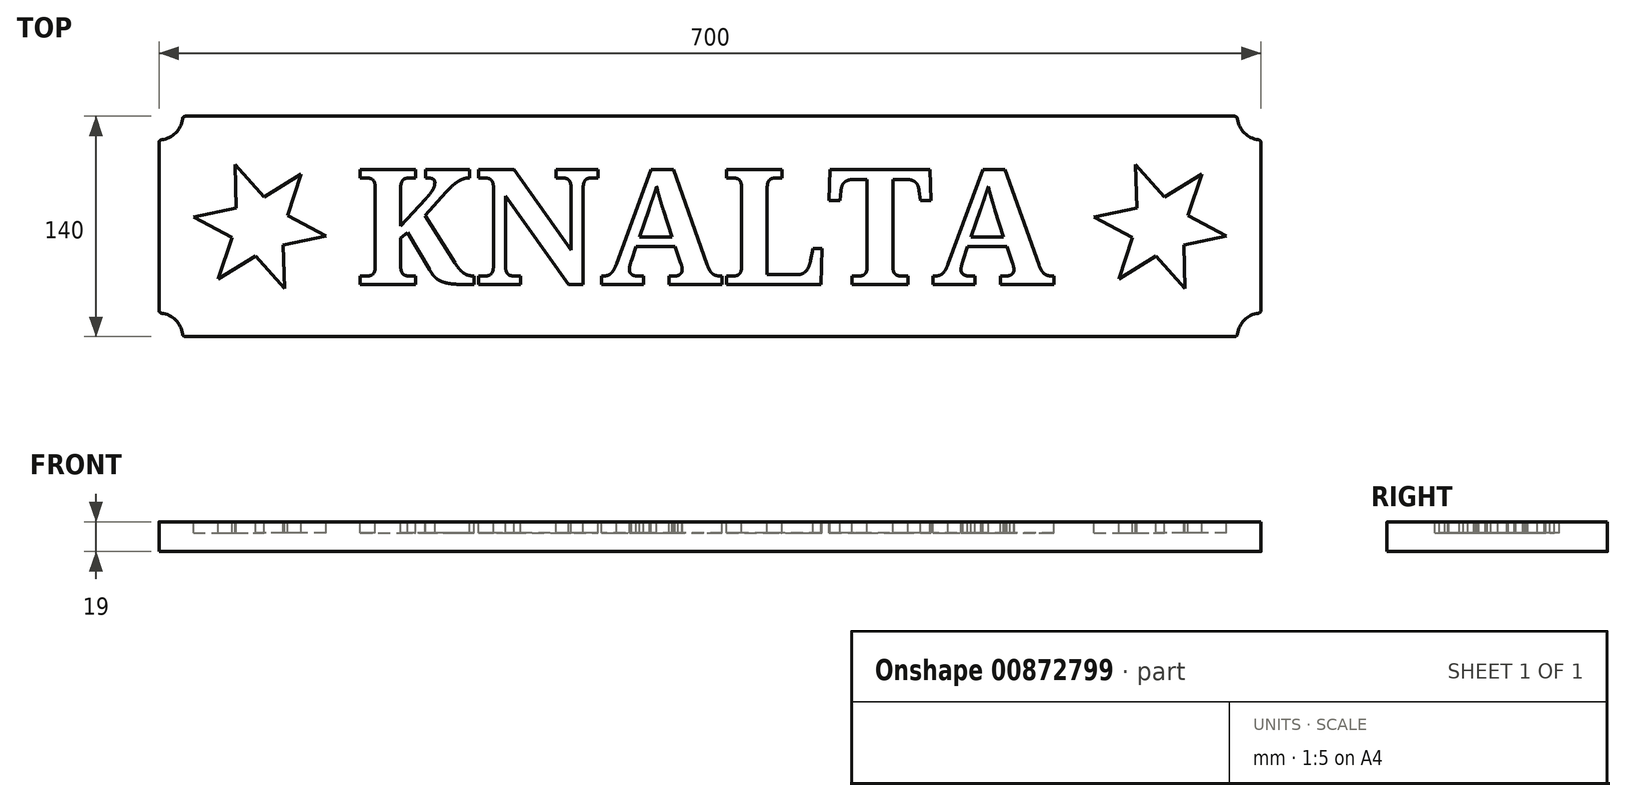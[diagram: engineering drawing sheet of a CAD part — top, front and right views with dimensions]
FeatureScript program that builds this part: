
annotation { "Feature Type Name" : "Feature", "Feature Type Description" : "" }
export const myFeature = defineFeature(function(context is Context, id is Id, definition is map)
    precondition{}
    {
        {
            var Q0;
            Q0=qCreatedBy(makeId("Top.planeOp"),FACE);
            var sketch = newSketch(context, id + "F0", { "sketchPlane" : qUnion([Q0])});
            skLineSegment(sketch, "E0", {"start": v(0, 459.17) * mm, "end": v(0, -526.61) * mm, "construction": true});
            skLineSegment(sketch, "E1", {"start": v(-506.97, 0) * mm, "end": v(534.36, 0) * mm, "construction": true});
            skLineSegment(sketch, "E2.bottom", {"start": v(-333.12, 70) * mm, "end": v(0, 70) * mm});
            skLineSegment(sketch, "E2.top", {"start": v(-350, 0) * mm, "end": v(0, 0) * mm});
            skLineSegment(sketch, "E2.left", {"start": v(-350, 53.12) * mm, "end": v(-350, 0) * mm});
            skLineSegment(sketch, "E2.right", {"start": v(0, 70) * mm, "end": v(0, 0) * mm});
            skArc(sketch, "E3", {"start": v(-348.24, 55.1) * mm, "mid": v(-339.4, 59.4) * mm, "end": v(-335.1, 68.24) * mm});
            skLineSegment(sketch, "E4.MirrorCS", {"start": v(350, 0) * mm, "end": v(0, 0) * mm});
            skLineSegment(sketch, "E5.MirrorCS", {"start": v(333.12, 70) * mm, "end": v(0, 70) * mm});
            skLineSegment(sketch, "E6.MirrorCS", {"start": v(350, 53.12) * mm, "end": v(350, 0) * mm});
            skArc(sketch, "E7.MirrorC", {"start": v(348.24, 55.1) * mm, "mid": v(339.4, 59.4) * mm, "end": v(335.1, 68.24) * mm});
            skLineSegment(sketch, "E8.MirrorCS", {"start": v(0, -70) * mm, "end": v(0, 0) * mm});
            skArc(sketch, "E9.MirrorC", {"start": v(-348.24, -55.1) * mm, "mid": v(-339.4, -59.4) * mm, "end": v(-335.1, -68.24) * mm});
            skLineSegment(sketch, "E10.MirrorCS", {"start": v(-333.12, -70) * mm, "end": v(0, -70) * mm});
            skLineSegment(sketch, "E11.MirrorCS", {"start": v(-350, -53.12) * mm, "end": v(-350, 0) * mm});
            skLineSegment(sketch, "E12.MirrorCS", {"start": v(350, -53.12) * mm, "end": v(350, 0) * mm});
            skLineSegment(sketch, "E13.MirrorCS", {"start": v(333.12, -70) * mm, "end": v(0, -70) * mm});
            skArc(sketch, "E14.MirrorC", {"start": v(348.24, -55.1) * mm, "mid": v(339.4, -59.4) * mm, "end": v(335.1, -68.24) * mm});
            skPoint(sketch, "E15.visualSharp", {"position": v(-335, 70) * mm});
            skArc(sketch, "E15.filletArc", {"start": v(-333.12, 70) * mm, "mid": v(-334.45, 69.5) * mm, "end": v(-335.1, 68.24) * mm});
            skPoint(sketch, "E16.visualSharp", {"position": v(-350, 55) * mm});
            skArc(sketch, "E16.filletArc", {"start": v(-348.24, 55.1) * mm, "mid": v(-349.5, 54.45) * mm, "end": v(-350, 53.12) * mm});
            skPoint(sketch, "E17.visualSharp", {"position": v(-350, -55) * mm});
            skArc(sketch, "E17.filletArc", {"start": v(-350, -53.12) * mm, "mid": v(-349.5, -54.45) * mm, "end": v(-348.24, -55.1) * mm});
            skPoint(sketch, "E18.visualSharp", {"position": v(-335, -70) * mm});
            skArc(sketch, "E18.filletArc", {"start": v(-335.1, -68.24) * mm, "mid": v(-334.45, -69.5) * mm, "end": v(-333.12, -70) * mm});
            skPoint(sketch, "E19.visualSharp", {"position": v(335, -70) * mm});
            skArc(sketch, "E19.filletArc", {"start": v(333.12, -70) * mm, "mid": v(334.45, -69.5) * mm, "end": v(335.1, -68.24) * mm});
            skPoint(sketch, "E20.visualSharp", {"position": v(350, -55) * mm});
            skArc(sketch, "E20.filletArc", {"start": v(348.24, -55.1) * mm, "mid": v(349.5, -54.45) * mm, "end": v(350, -53.12) * mm});
            skPoint(sketch, "E21.visualSharp", {"position": v(350, 55) * mm});
            skArc(sketch, "E21.filletArc", {"start": v(350, 53.12) * mm, "mid": v(349.5, 54.45) * mm, "end": v(348.24, 55.1) * mm});
            skPoint(sketch, "E22.visualSharp", {"position": v(335, 70) * mm});
            skArc(sketch, "E22.filletArc", {"start": v(335.1, 68.24) * mm, "mid": v(334.45, 69.5) * mm, "end": v(333.12, 70) * mm});
            skSolve(sketch);
        }
        {
            var Q0;
            Q0 = qSketchRegion(id + "F0", true);
            extrude(context, id + "F1", {"entities" : qUnion([Q0]), "depth" : 19 * mm, "offsetDistance" : 25 * mm});
        }
        {
            var Q0;
            Q0=makeQuery(id+"F1.opExtrude","CAP_FACE",FACE,{"disambiguationData":[OSD([sQuery(id+"F0.wireOp",EDGE,"E2.bottom"),sQuery(id+"F0.wireOp",EDGE,"E2.left"),sQuery(id+"F0.wireOp",EDGE,"E3"),sQuery(id+"F0.wireOp",EDGE,"E5.MirrorCS"),sQuery(id+"F0.wireOp",EDGE,"E6.MirrorCS"),sQuery(id+"F0.wireOp",EDGE,"E7.MirrorC"),sQuery(id+"F0.wireOp",EDGE,"E9.MirrorC"),sQuery(id+"F0.wireOp",EDGE,"E10.MirrorCS"),sQuery(id+"F0.wireOp",EDGE,"E11.MirrorCS"),sQuery(id+"F0.wireOp",EDGE,"E12.MirrorCS"),sQuery(id+"F0.wireOp",EDGE,"E13.MirrorCS"),sQuery(id+"F0.wireOp",EDGE,"E14.MirrorC")])],"isStart":false});
            var sketch = newSketch(context, id + "F2", { "sketchPlane" : qUnion([Q0])});
            skPoint(sketch, "E23.0.midPoint", {"position": v(-257.12, -22.82) * mm});
            skLineSegment(sketch, "E24", {"start": v(-301.7, 39.5) * mm, "end": v(-300.89, 11.76) * mm});
            skLineSegment(sketch, "E25", {"start": v(-301.7, 39.5) * mm, "end": v(-283.26, 18.78) * mm});
            skLineSegment(sketch, "E26", {"start": v(-328.05, 6.14) * mm, "end": v(-303.63, -7.01) * mm});
            skLineSegment(sketch, "E27", {"start": v(-328.05, 6.14) * mm, "end": v(-300.89, 11.76) * mm});
            skLineSegment(sketch, "E28", {"start": v(-270.3, -39.5) * mm, "end": v(-271.11, -11.76) * mm});
            skLineSegment(sketch, "E29", {"start": v(-270.3, -39.5) * mm, "end": v(-288.74, -18.78) * mm});
            skLineSegment(sketch, "E30", {"start": v(-312.35, -33.35) * mm, "end": v(-288.74, -18.78) * mm});
            skLineSegment(sketch, "E31", {"start": v(-312.35, -33.35) * mm, "end": v(-303.63, -7.01) * mm});
            skLineSegment(sketch, "E32", {"start": v(-259.65, 33.35) * mm, "end": v(-283.26, 18.78) * mm});
            skLineSegment(sketch, "E33", {"start": v(-259.65, 33.35) * mm, "end": v(-268.37, 7.01) * mm});
            skLineSegment(sketch, "E34", {"start": v(-243.95, -6.14) * mm, "end": v(-268.37, 7.01) * mm});
            skLineSegment(sketch, "E35", {"start": v(-243.95, -6.14) * mm, "end": v(-271.11, -11.76) * mm});
            skPoint(sketch, "E36.center.orphan", {"position": v(-286, 0) * mm});
            skCircle(sketch, "E37", {"center": v(-286, 0) * mm, "radius": 18.98 * mm, "construction": true});
            skCircle(sketch, "E38", {"center": v(-286, 0) * mm, "radius": 42.5 * mm, "construction": true});
            skPoint(sketch, "E39.0.midPoint", {"position": v(314.88, -22.82) * mm});
            skLineSegment(sketch, "E40", {"start": v(270.3, 39.5) * mm, "end": v(271.11, 11.76) * mm});
            skLineSegment(sketch, "E41", {"start": v(270.3, 39.5) * mm, "end": v(288.74, 18.78) * mm});
            skLineSegment(sketch, "E42", {"start": v(243.95, 6.14) * mm, "end": v(268.37, -7.01) * mm});
            skLineSegment(sketch, "E43", {"start": v(243.95, 6.14) * mm, "end": v(271.11, 11.76) * mm});
            skLineSegment(sketch, "E44", {"start": v(301.7, -39.5) * mm, "end": v(300.89, -11.76) * mm});
            skLineSegment(sketch, "E45", {"start": v(301.7, -39.5) * mm, "end": v(283.26, -18.78) * mm});
            skLineSegment(sketch, "E46", {"start": v(259.65, -33.35) * mm, "end": v(283.26, -18.78) * mm});
            skLineSegment(sketch, "E47", {"start": v(259.65, -33.35) * mm, "end": v(268.37, -7.01) * mm});
            skLineSegment(sketch, "E48", {"start": v(312.35, 33.35) * mm, "end": v(288.74, 18.78) * mm});
            skLineSegment(sketch, "E49", {"start": v(312.35, 33.35) * mm, "end": v(303.63, 7.01) * mm});
            skLineSegment(sketch, "E50", {"start": v(328.05, -6.14) * mm, "end": v(303.63, 7.01) * mm});
            skLineSegment(sketch, "E51", {"start": v(328.05, -6.14) * mm, "end": v(300.89, -11.76) * mm});
            skPoint(sketch, "E52.center.orphan", {"position": v(286, 0) * mm});
            skCircle(sketch, "E53", {"center": v(286, 0) * mm, "radius": 18.98 * mm, "construction": true});
            skCircle(sketch, "E54", {"center": v(286, 0) * mm, "radius": 42.5 * mm, "construction": true});
            skText(sketch, "E55", { "text": "KNALTA", "fontName": "NotoSerif-Bold.ttf"});
            const initialGuessF2  = {"E55": [-0.225, -0.03685, 1, 0, 0.07365]};
            skSetInitialGuess(sketch, initialGuessF2);
            skSolve(sketch);
        }
        {
            var Q0;
            Q0 = qSketchRegion(id + "F2", true);
            extrude(context, id + "F3", {"entities" : qUnion([Q0]), "operationType" : NewBodyOperationType.REMOVE, "oppositeDirection" : true, "depth" : 7 * mm, "offsetDistance" : 25 * mm});
        }
    });
